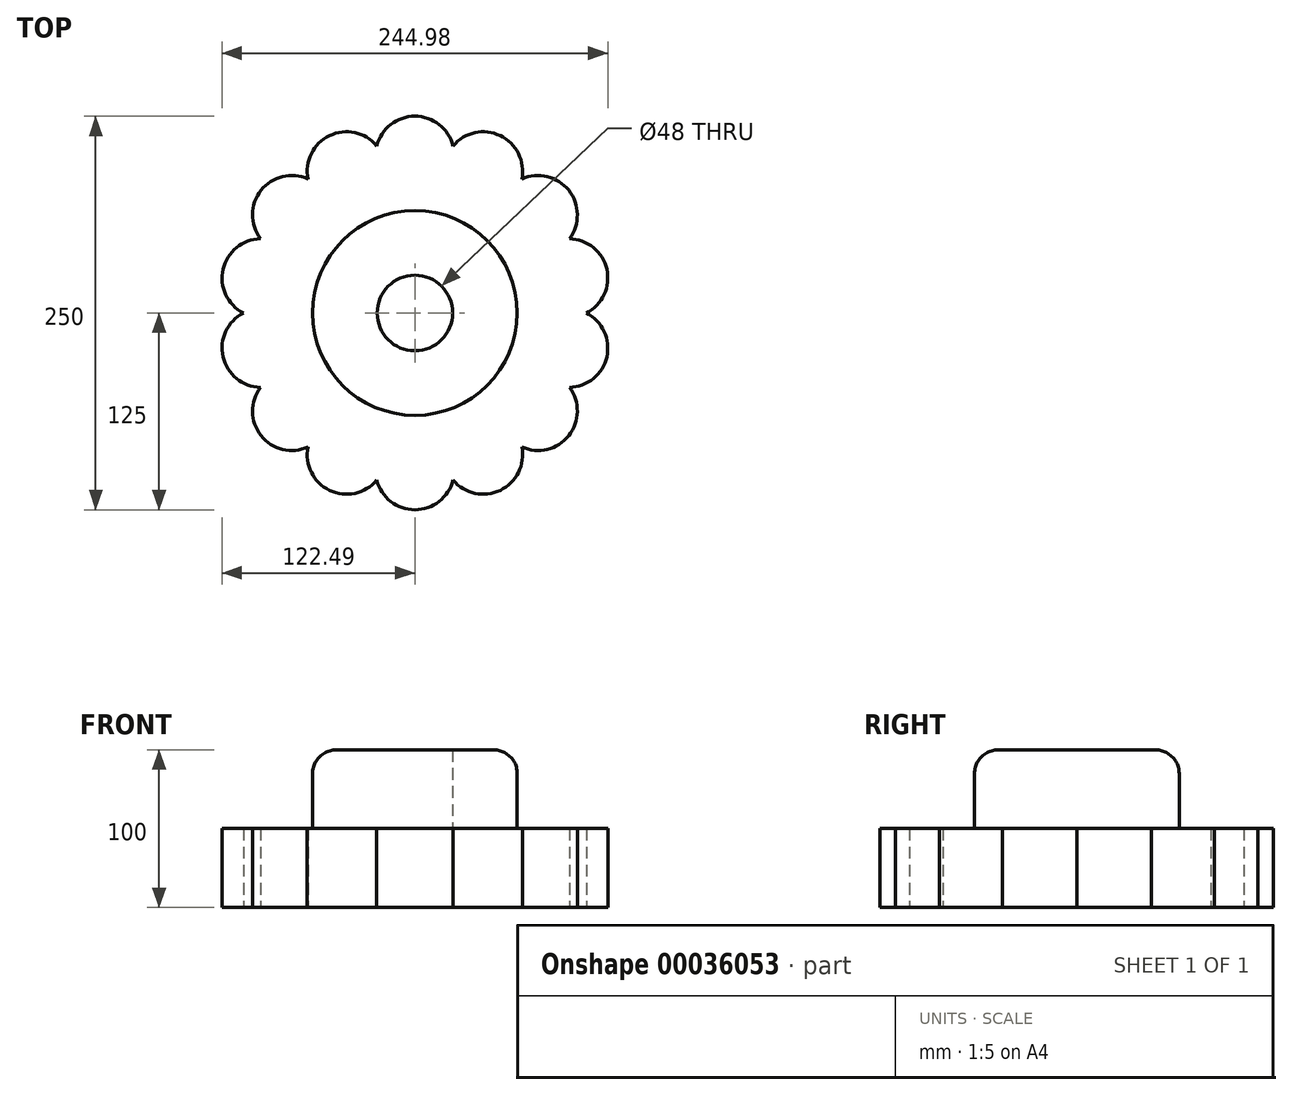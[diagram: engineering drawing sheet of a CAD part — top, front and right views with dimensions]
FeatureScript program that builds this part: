
annotation { "Feature Type Name" : "Feature", "Feature Type Description" : "" }
export const myFeature = defineFeature(function(context is Context, id is Id, definition is map)
    precondition{}
    {
        {
            var Q0;
            Q0=qCreatedBy(makeId("Top.planeOp"),FACE);
            var sketch = newSketch(context, id + "F0", { "sketchPlane" : qUnion([Q0])});
            skCircle(sketch, "E0", {"center": v(0, 0) * mm, "radius": 24 * mm});
            skArc(sketch, "E1", {"start": v(24.23, 106.16) * mm, "mid": v(0, 125) * mm, "end": v(-24.23, 106.16) * mm});
            skArc(sketch, "E2.3.0", {"start": v(-98.1, 47.24) * mm, "mid": v(-121.87, 27.82) * mm, "end": v(-108.89, 0) * mm});
            skArc(sketch, "E2.4.0", {"start": v(-108.89, 0) * mm, "mid": v(-121.87, -27.82) * mm, "end": v(-98.1, -47.24) * mm});
            skArc(sketch, "E2.5.0", {"start": v(-98.1, -47.24) * mm, "mid": v(-97.73, -77.94) * mm, "end": v(-67.9, -85.13) * mm});
            skArc(sketch, "E2.6.0", {"start": v(-67.9, -85.13) * mm, "mid": v(-54.24, -112.62) * mm, "end": v(-24.23, -106.16) * mm});
            skArc(sketch, "E2.7.0", {"start": v(-24.23, -106.16) * mm, "mid": v(0, -125) * mm, "end": v(24.23, -106.16) * mm});
            skArc(sketch, "E2.8.0", {"start": v(24.23, -106.16) * mm, "mid": v(54.24, -112.62) * mm, "end": v(67.9, -85.13) * mm});
            skArc(sketch, "E2.9.0", {"start": v(67.9, -85.13) * mm, "mid": v(97.73, -77.94) * mm, "end": v(98.1, -47.24) * mm});
            skArc(sketch, "E2.10.0", {"start": v(98.1, -47.24) * mm, "mid": v(121.87, -27.82) * mm, "end": v(108.89, 0) * mm});
            skArc(sketch, "E2.11.0", {"start": v(108.89, 0) * mm, "mid": v(121.87, 27.82) * mm, "end": v(98.1, 47.24) * mm});
            skArc(sketch, "E2.12.0", {"start": v(98.1, 47.24) * mm, "mid": v(97.73, 77.94) * mm, "end": v(67.9, 85.13) * mm});
            skArc(sketch, "E2.13.0", {"start": v(67.9, 85.13) * mm, "mid": v(54.24, 112.62) * mm, "end": v(24.23, 106.16) * mm});
            skArc(sketch, "E3.trimOffspring", {"start": v(-67.9, 85.13) * mm, "mid": v(-97.73, 77.94) * mm, "end": v(-98.1, 47.24) * mm});
            skArc(sketch, "E4.trimOffspring", {"start": v(-24.23, 106.16) * mm, "mid": v(-54.24, 112.62) * mm, "end": v(-67.9, 85.13) * mm});
            skSolve(sketch);
        }
        {
            var Q0;
            Q0=makeQuery(id+"F0.imprint","IMPRINT",FACE,{"disambiguationData":[TD([[makeQuery(id+"F0.imprint","IMPRINT",EDGE,{"derivedFrom":sQuery(id+"F0.wireOp",EDGE,"E0")}),-1.0]])]});
            extrude(context, id + "F1", {"entities" : qUnion([Q0]), "depth" : 50 * mm});
        }
        {
            var Q0;
            Q0=makeQuery(id+"F1.opExtrude","CAP_FACE",FACE,{"disambiguationData":[OSD([sQuery(id+"F0.wireOp",EDGE,"E0"),sQuery(id+"F0.wireOp",EDGE,"E1"),sQuery(id+"F0.wireOp",EDGE,"E2.3.0"),sQuery(id+"F0.wireOp",EDGE,"E2.4.0"),sQuery(id+"F0.wireOp",EDGE,"E2.5.0"),sQuery(id+"F0.wireOp",EDGE,"E2.6.0"),sQuery(id+"F0.wireOp",EDGE,"E2.7.0"),sQuery(id+"F0.wireOp",EDGE,"E2.8.0"),sQuery(id+"F0.wireOp",EDGE,"E2.9.0"),sQuery(id+"F0.wireOp",EDGE,"E2.10.0"),sQuery(id+"F0.wireOp",EDGE,"E2.11.0"),sQuery(id+"F0.wireOp",EDGE,"E2.12.0"),sQuery(id+"F0.wireOp",EDGE,"E2.13.0"),sQuery(id+"F0.wireOp",EDGE,"E3.trimOffspring"),sQuery(id+"F0.wireOp",EDGE,"E4.trimOffspring")])],"isStart":false});
            var sketch = newSketch(context, id + "F2", { "sketchPlane" : qUnion([Q0])});
            skCircle(sketch, "E5", {"center": v(0, 0) * mm, "radius": 24 * mm});
            skCircle(sketch, "E6", {"center": v(0, 0) * mm, "radius": 65 * mm});
            skSolve(sketch);
        }
        {
            var Q0;
            Q0 = qSketchRegion(id + "F2", true);
            extrude(context, id + "F3", {"entities" : qUnion([Q0]), "operationType" : NewBodyOperationType.ADD, "depth" : 50 * mm});
        }
        {
            var Q0;
            Q0=makeQuery(id+"F3.opExtrude","CAP_EDGE",EDGE,{"disambiguationData":[OSD([sQuery(id+"F2.wireOp",EDGE,"E6")])],"isStart":true});
            var Q1;
            Q1=makeQuery(id+"F3.opExtrude","CAP_EDGE",EDGE,{"disambiguationData":[OSD([sQuery(id+"F2.wireOp",EDGE,"E6")])],"isStart":false});
            fillet(context, id + "F4", {"entities" : qUnion([Q0, Q1]), "radius" : 15 * mm, "tangentPropagation" : true, "allowEdgeOverflow" : false});
        }
    });
